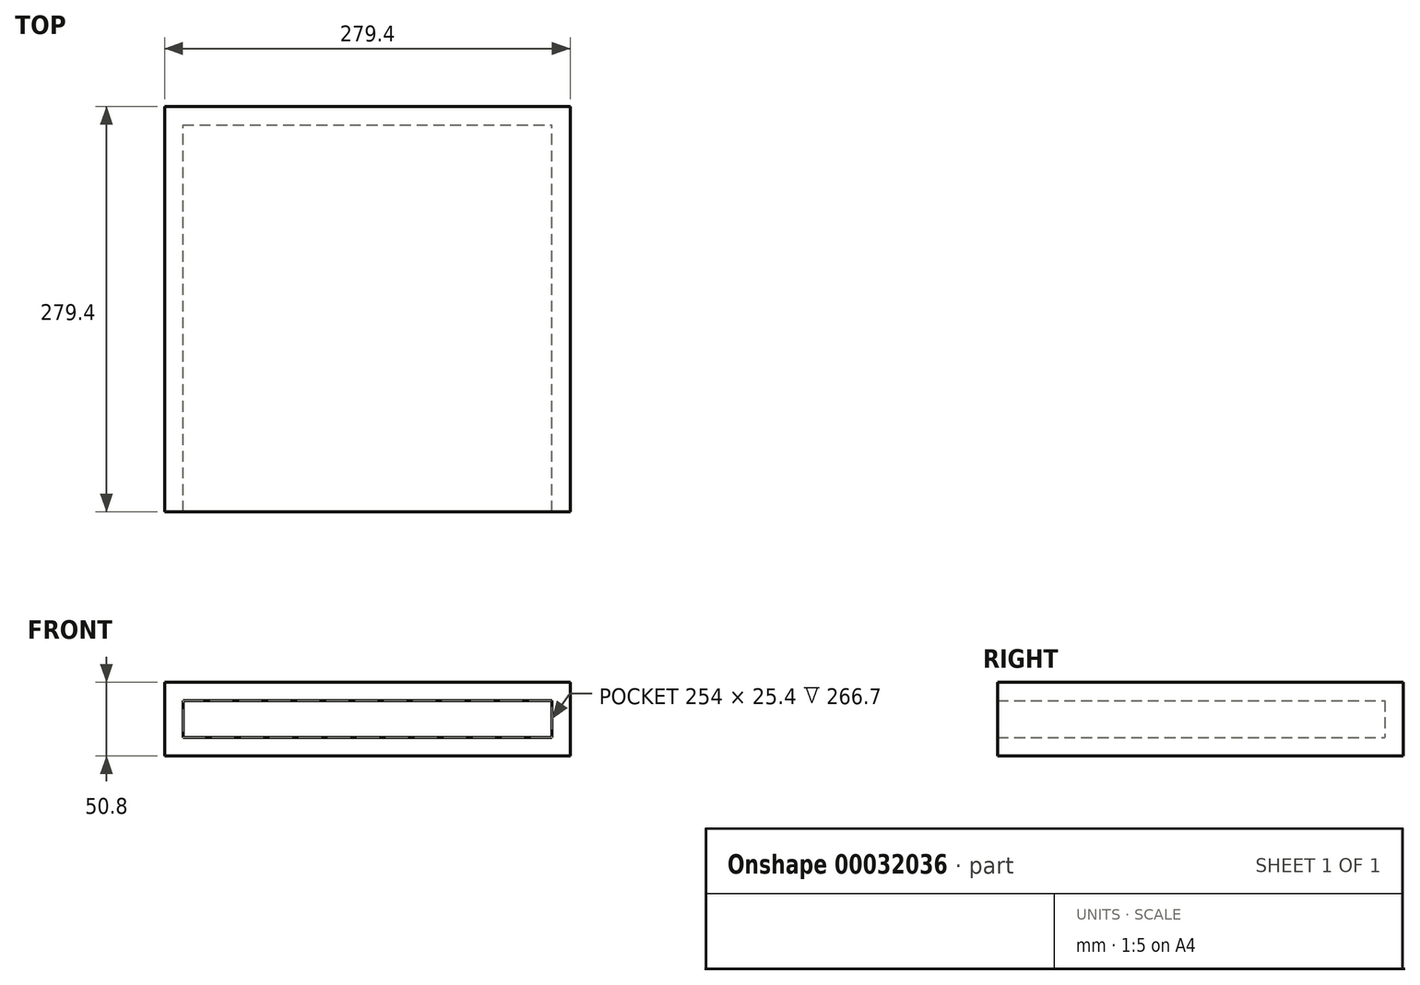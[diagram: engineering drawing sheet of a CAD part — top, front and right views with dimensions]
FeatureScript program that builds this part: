
annotation { "Feature Type Name" : "Feature", "Feature Type Description" : "" }
export const myFeature = defineFeature(function(context is Context, id is Id, definition is map)
    precondition{}
    {
        {
            var Q0;
            Q0=qCreatedBy(makeId("Top.planeOp"),FACE);
            var sketch = newSketch(context, id + "F0", { "sketchPlane" : qUnion([Q0])});
            skLineSegment(sketch, "E0.rect.bottom", {"start": v(190.5, 190.5) * mm, "end": v(-190.5, 190.5) * mm});
            skLineSegment(sketch, "E0.rect.top", {"start": v(190.5, -190.5) * mm, "end": v(-190.5, -190.5) * mm});
            skLineSegment(sketch, "E0.rect.left", {"start": v(190.5, 190.5) * mm, "end": v(190.5, -190.5) * mm});
            skLineSegment(sketch, "E0.rect.right", {"start": v(-190.5, 190.5) * mm, "end": v(-190.5, -190.5) * mm});
            skPoint(sketch, "E0.rect.middle", {"position": v(0, 0) * mm});
            skLineSegment(sketch, "E1.bottom", {"start": v(-190.5, -190.5) * mm, "end": v(-139.7, -190.5) * mm});
            skLineSegment(sketch, "E1.top", {"start": v(-190.5, -139.7) * mm, "end": v(-139.7, -139.7) * mm});
            skLineSegment(sketch, "E1.left", {"start": v(-190.5, -190.5) * mm, "end": v(-190.5, -139.7) * mm});
            skLineSegment(sketch, "E1.right", {"start": v(-139.7, -190.5) * mm, "end": v(-139.7, -139.7) * mm});
            skLineSegment(sketch, "E2.bottom", {"start": v(190.5, -190.5) * mm, "end": v(139.7, -190.5) * mm});
            skLineSegment(sketch, "E2.top", {"start": v(190.5, -139.7) * mm, "end": v(139.7, -139.7) * mm});
            skLineSegment(sketch, "E2.left", {"start": v(190.5, -190.5) * mm, "end": v(190.5, -139.7) * mm});
            skLineSegment(sketch, "E2.right", {"start": v(139.7, -190.5) * mm, "end": v(139.7, -139.7) * mm});
            skLineSegment(sketch, "E3.bottom", {"start": v(-190.5, 190.5) * mm, "end": v(-139.7, 190.5) * mm});
            skLineSegment(sketch, "E3.top", {"start": v(-190.5, 139.7) * mm, "end": v(-139.7, 139.7) * mm});
            skLineSegment(sketch, "E3.left", {"start": v(-190.5, 190.5) * mm, "end": v(-190.5, 139.7) * mm});
            skLineSegment(sketch, "E3.right", {"start": v(-139.7, 190.5) * mm, "end": v(-139.7, 139.7) * mm});
            skLineSegment(sketch, "E4.bottom", {"start": v(-139.7, -139.7) * mm, "end": v(-127, -139.7) * mm});
            skLineSegment(sketch, "E4.top", {"start": v(-139.7, 139.7) * mm, "end": v(-127, 139.7) * mm});
            skLineSegment(sketch, "E4.left", {"start": v(-139.7, -139.7) * mm, "end": v(-139.7, 139.7) * mm});
            skLineSegment(sketch, "E4.right", {"start": v(-127, -139.7) * mm, "end": v(-127, 139.7) * mm});
            skLineSegment(sketch, "E5.bottom", {"start": v(-127, 139.7) * mm, "end": v(139.7, 139.7) * mm});
            skLineSegment(sketch, "E5.top", {"start": v(-127, 127) * mm, "end": v(139.7, 127) * mm});
            skLineSegment(sketch, "E5.left", {"start": v(-127, 139.7) * mm, "end": v(-127, 127) * mm});
            skLineSegment(sketch, "E5.right", {"start": v(139.7, 139.7) * mm, "end": v(139.7, 127) * mm});
            skLineSegment(sketch, "E6.bottom", {"start": v(139.7, -139.7) * mm, "end": v(127, -139.7) * mm});
            skLineSegment(sketch, "E6.top", {"start": v(139.7, 127) * mm, "end": v(127, 127) * mm});
            skLineSegment(sketch, "E6.left", {"start": v(139.7, -139.7) * mm, "end": v(139.7, 127) * mm});
            skLineSegment(sketch, "E6.right", {"start": v(127, -139.7) * mm, "end": v(127, 127) * mm});
            skSolve(sketch);
        }
        {
            var Q0;
            Q0=makeQuery(id+"F0.imprint","IMPRINT",FACE,{"disambiguationData":[TD([[makeQuery(id+"F0.imprint","IMPRINT",EDGE,{"derivedFrom":sQuery(id+"F0.wireOp",EDGE,"E4.bottom")}),1.0]])]});
            var Q1;
            Q1=makeQuery(id+"F0.imprint","IMPRINT",FACE,{"disambiguationData":[TD([[makeQuery(id+"F0.imprint","IMPRINT",EDGE,{"derivedFrom":sQuery(id+"F0.wireOp",EDGE,"E5.bottom")}),-1.0]])]});
            var Q2;
            Q2=makeQuery(id+"F0.imprint","IMPRINT",FACE,{"disambiguationData":[TD([[makeQuery(id+"F0.imprint","IMPRINT",EDGE,{"derivedFrom":sQuery(id+"F0.wireOp",EDGE,"E6.bottom")}),-1.0]])]});
            extrude(context, id + "F1", {"entities" : qUnion([Q0, Q1, Q2]), "depth" : 50.8 * mm});
        }
        {
            var Q0;
            Q0=makeQuery(id+"F1.opExtrude","SWEPT_FACE",FACE,{"disambiguationData":[OSD([sQuery(id+"F0.wireOp",EDGE,"E5.top")])]});
            var sketch = newSketch(context, id + "F2", { "sketchPlane" : qUnion([Q0])});
            skLineSegment(sketch, "E7", {"start": v(-127, 50.8) * mm, "end": v(-127, 38.1) * mm});
            skLineSegment(sketch, "E8.bottom", {"start": v(-127, 38.1) * mm, "end": v(127, 38.1) * mm});
            skLineSegment(sketch, "E8.top", {"start": v(-127, 50.8) * mm, "end": v(127, 50.8) * mm});
            skLineSegment(sketch, "E8.left", {"start": v(-127, 38.1) * mm, "end": v(-127, 50.8) * mm});
            skLineSegment(sketch, "E8.right", {"start": v(127, 38.1) * mm, "end": v(127, 50.8) * mm});
            skSolve(sketch);
        }
        {
            var Q0;
            Q0=makeQuery(id+"F2.imprint","IMPRINT",FACE,{"disambiguationData":[TD([[makeQuery(id+"F2.imprint","IMPRINT",EDGE,{"derivedFrom":sQuery(id+"F2.wireOp",EDGE,"E8.bottom")}),1.0]])]});
            extrude(context, id + "F3", {"entities" : qUnion([Q0]), "operationType" : NewBodyOperationType.ADD, "depth" : 266.7 * mm});
        }
        {
            var Q0;
            Q0=makeQuery(id+"F1.opExtrude","SWEPT_FACE",FACE,{"disambiguationData":[OSD([sQuery(id+"F0.wireOp",EDGE,"E5.top")])]});
            var sketch = newSketch(context, id + "F4", { "sketchPlane" : qUnion([Q0])});
            skLineSegment(sketch, "E9", {"start": v(-127, 0) * mm, "end": v(-127, 12.7) * mm});
            skLineSegment(sketch, "E10.bottom", {"start": v(-127, 12.7) * mm, "end": v(127, 12.7) * mm});
            skLineSegment(sketch, "E10.top", {"start": v(-127, 0) * mm, "end": v(127, 0) * mm});
            skLineSegment(sketch, "E10.left", {"start": v(-127, 12.7) * mm, "end": v(-127, 0) * mm});
            skLineSegment(sketch, "E10.right", {"start": v(127, 12.7) * mm, "end": v(127, 0) * mm});
            skSolve(sketch);
        }
        {
            var Q0;
            Q0=makeQuery(id+"F4.imprint","IMPRINT",FACE,{"disambiguationData":[TD([[makeQuery(id+"F4.imprint","IMPRINT",EDGE,{"derivedFrom":sQuery(id+"F4.wireOp",EDGE,"E10.bottom")}),-1.0]])]});
            extrude(context, id + "F5", {"entities" : qUnion([Q0]), "operationType" : NewBodyOperationType.ADD, "depth" : 266.7 * mm});
        }
    });
